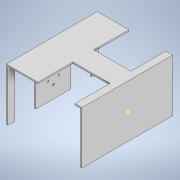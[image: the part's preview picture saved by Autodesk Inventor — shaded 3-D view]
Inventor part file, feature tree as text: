
AUTODESK INVENTOR PART (.ipt)
format: ipt  version: 2020 (Build 240168000, 168)  size: 307,712 bytes
history: native  units: in
note: dims shown in document units (in); Inventor stores cm internally (conversion verified against a paired STEP export)
features: sketch x18, extrude x16
ambient origin geometry x8: Origin, YZ Plane, XZ Plane, XY Plane, X Axis, Y Axis, Z Axis, Center Point
bodies: Solid1 (feature_tree)
feature tree (34):
  extrude  "Extrusion1"  Depth=3.75in
  extrude  "Extrusion3"  Depth=1.5in
  sketch  "Sketch4"  dims[d13=2.5in d14=510.35in d15=0.0in]
  extrude  "Extrusion4"  Depth=2.5in TaperAngle=0.0deg
  sketch  "Sketch6"  dims[d18=8.0in d19=0.0in d20=1.0in d21=0.0in]
  extrude  "Extrusion5"  Depth=0.1in
  extrude  "Extrusion6"  Depth=1.0in TaperAngle=0.0deg
  extrude  "Extrusion7"  Depth=2.0in
  extrude  "Extrusion8"  Depth=1.5in
  extrude  "Extrusion9"  Depth=1.5in
  extrude  "Extrusion10"  Depth=0.25in
  extrude  "Extrusion11"  Depth=0.1in TaperAngle=0.0deg
  extrude  "Extrusion12"  Depth=0.1in TaperAngle=0.0deg
  extrude  "Extrusion13"  Depth=0.5in
  extrude  "Extrusion14"  Depth=0.1in TaperAngle=0.0deg
  extrude  "Extrusion15"  Depth=0.5in
  extrude  "Extrusion16"  Depth=0.1in TaperAngle=0.0deg
  extrude  "Extrusion17"  Depth=0.1406in
  sketch  "Sketch1"  dims[d0=6.5in d1=3.75in]
  sketch  "Sketch3"  dims[d2=5.45in d3=0.0in d12=1.5in]
  sketch  "Sketch5"  dims[d16=0.1in d17=0.1in]
  sketch  "Sketch7"  dims[d22=0.25in d23=2.0in]
  sketch  "Sketch8"  dims[d24=0.25in d25=1.5in]
  sketch  "Sketch9"  dims[d26=0.5in d27=1.5in]
  sketch  "Sketch10"  dims[d28=1.0in d29=0.0in d30=0.25in]
  sketch  "Sketch11"  dims[d31=0.25in d32=0.1in d33=0.0in]
  sketch  "Sketch12"  dims[d34=3.5in d35=0.1in d36=0.0in]
  sketch  "Sketch13"  dims[d37=0.5in d38=0.5in]
  sketch  "Sketch14"  dims[d39=0.5in d40=0.1in d41=0.0in]
  sketch  "Sketch15"  dims[d42=0.5in d43=0.5in]
  sketch  "Sketch16"  dims[d44=0.1in d45=0.0in d46=0.1in d47=0.0in]
  sketch  "Sketch17"  dims[d49=0.1406in d50=0.1406in]
  sketch  "Sketch18"  dims[d51=0.1406in]
  sketch  "Sketch19"  dims[d52=0.1406in d53=0.1in d54=0.0in d55=6.0in d56=0.0in d57=1.75in d58=0.1in d59=0.0in d60=0.05in d61=0.1in d62=6.5in d63=0.0in d64=0.05in d65=6.5in d66=0.0in d67=0.05in d68=0.0in]
